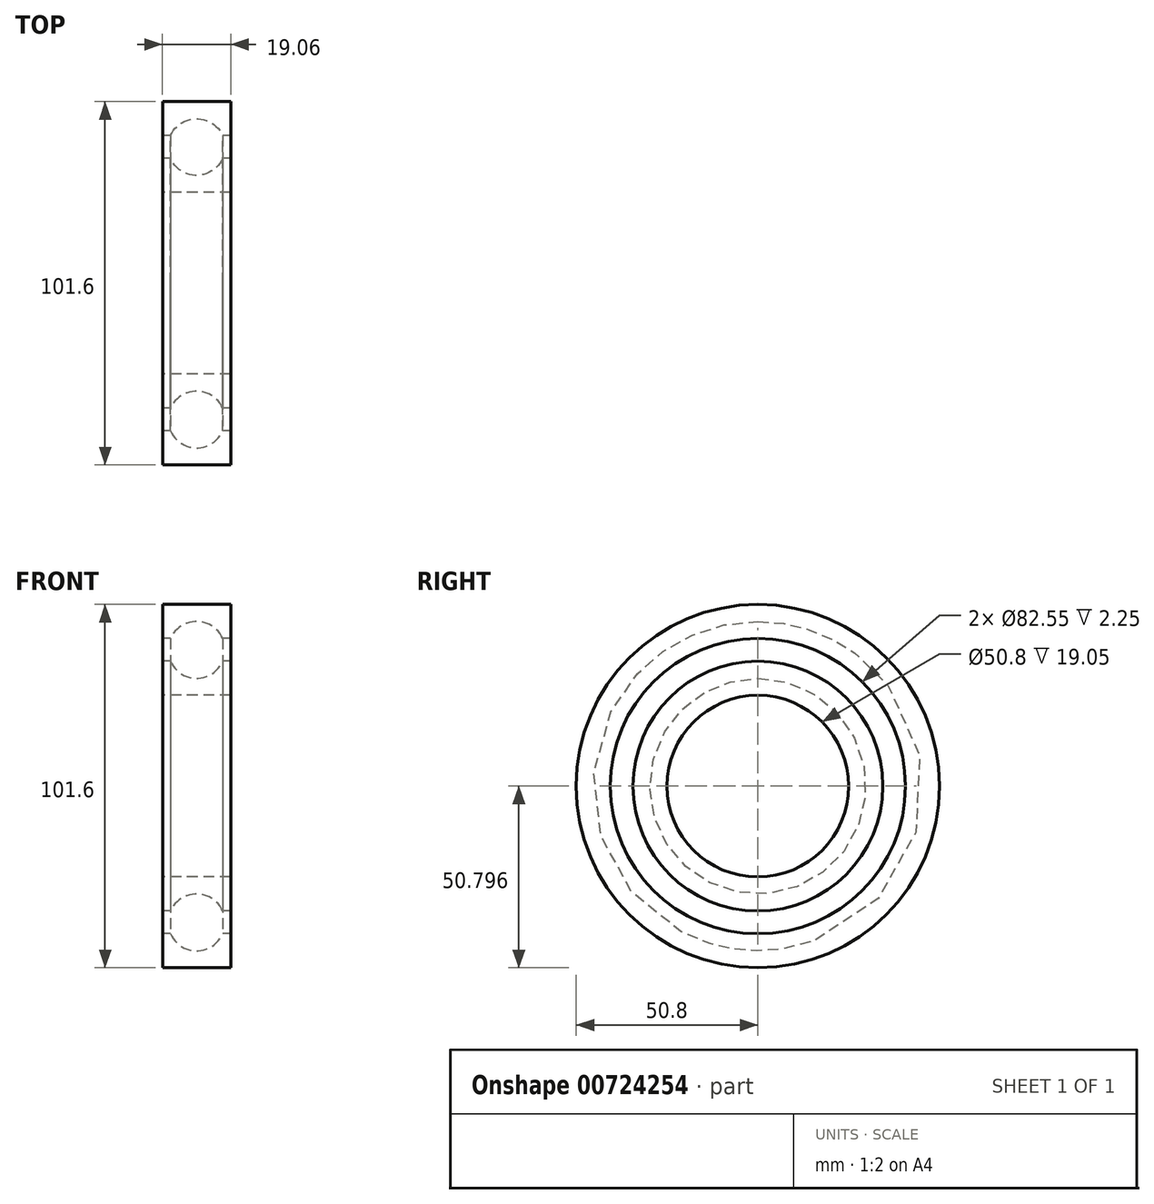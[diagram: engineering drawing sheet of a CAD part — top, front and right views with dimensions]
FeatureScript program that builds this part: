
annotation { "Feature Type Name" : "Feature", "Feature Type Description" : "" }
export const myFeature = defineFeature(function(context is Context, id is Id, definition is map)
    precondition{}
    {
        {
            var Q0;
            Q0=qCreatedBy(makeId("Front.planeOp"),FACE);
            var sketch = newSketch(context, id + "F0", { "sketchPlane" : qUnion([Q0])});
            skLineSegment(sketch, "E0.bottom", {"start": v(-9.52, 17.1) * mm, "end": v(9.53, 17.1) * mm});
            skLineSegment(sketch, "E0.top", {"start": v(-9.52, 7.57) * mm, "end": v(9.53, 7.57) * mm});
            skLineSegment(sketch, "E0.left", {"start": v(-9.52, 17.1) * mm, "end": v(-9.52, 7.57) * mm});
            skLineSegment(sketch, "E0.right", {"start": v(9.53, 17.1) * mm, "end": v(9.53, 7.57) * mm});
            skLineSegment(sketch, "E1.bottom", {"start": v(-9.52, 1.22) * mm, "end": v(9.53, 1.22) * mm});
            skLineSegment(sketch, "E1.top", {"start": v(-9.52, -8.3) * mm, "end": v(9.53, -8.3) * mm});
            skLineSegment(sketch, "E1.left", {"start": v(-9.52, 1.22) * mm, "end": v(-9.52, -8.3) * mm});
            skLineSegment(sketch, "E1.right", {"start": v(9.53, 1.22) * mm, "end": v(9.53, -8.3) * mm});
            skLineSegment(sketch, "E2", {"start": v(-9.52, -33.7) * mm, "end": v(9.53, -33.7) * mm, "construction": true});
            skLineSegment(sketch, "E3", {"start": v(0, 7.57) * mm, "end": v(0, 1.22) * mm, "construction": true});
            skCircle(sketch, "E4", {"center": v(0, 4.4) * mm, "radius": 7.94 * mm});
            skLineSegment(sketch, "E5", {"start": v(0, -33.7) * mm, "end": v(0, 4.4) * mm, "construction": true});
            skLineSegment(sketch, "E6", {"start": v(0, -3.54) * mm, "end": v(0, 12.33) * mm});
            skSolve(sketch);
        }
        {
            var Q0;
            Q0=makeQuery(id+"F0.imprint","IMPRINT",FACE,{"disambiguationData":[TD([[makeQuery(id+"F0.imprint","IMPRINT",EDGE,{"derivedFrom":sQuery(id+"F0.wireOp",EDGE,"E0.bottom")}),-1.0]])]});
            var Q1;
            Q1=makeQuery(id+"F0.imprint","IMPRINT",FACE,{"disambiguationData":[TD([[makeQuery(id+"F0.imprint","IMPRINT",EDGE,{"derivedFrom":sQuery(id+"F0.wireOp",EDGE,"E1.top")}),1.0]])]});
            var Q2;
            Q2=sQuery(id+"F0.wireOp",EDGE,"E2");
            revolve(context, id + "F1", {"surfaceOperationType" : NewSurfaceOperationType.NEW, "entities" : qUnion([Q0, Q1]), "axis" : qUnion([Q2]), "revolveType" : RevolveType.FULL});
        }
    });
